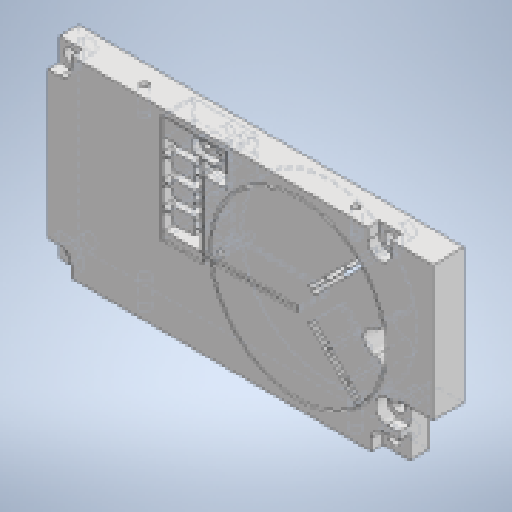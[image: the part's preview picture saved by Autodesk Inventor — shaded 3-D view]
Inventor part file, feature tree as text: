
AUTODESK INVENTOR PART (.ipt)
format: ipt  version: 2023 (Build 270158000, 158)  size: 611,328 bytes
history: native  units: mm
features: extrude x11, sketch x11, other x7, reference x7, fillet x1
ambient origin geometry x8: Origin, YZ Plane, XZ Plane, XY Plane, X Axis, Y Axis, Z Axis, Center Point
bodies: Solid1 (feature_tree)
feature tree (37):
  other  "<userpath>\ClawdDrive\Objet3D\IminaProbe\V3Roue\Settings.xlsx"
  extrude  "Extrusion1"  Depth=9.0mm
  extrude  "Extrusion2"  Depth=9.0mm TaperAngle=0.0deg
  extrude  "Extrusion3"  Depth=40.0mm
  fillet  "Fillet1"  Radius=1.6mm
  extrude  "Extrusion4"  Depth=45.0mm
  extrude  "Extrusion5"  TaperAngle=45.0deg  [1 undecoded]
  extrude  "Extrusion6"  Depth=10.0mm
  extrude  "Extrusion7"  Depth=1.0mm
  extrude  "Extrusion8"  Depth=1.0mm
  extrude  "Extrusion9"  Depth=0.05mm
  extrude  "Extrusion10"  Depth=0.1mm
  extrude  "Extrusion11"  Depth=10.0mm TaperAngle=0.0deg
  sketch  "Sketch1"  dims[d0=8.0mm d1=0.0mm d2=9.0mm]
  reference  "Reference1"
  sketch  "Sketch2"  dims[d3=15.0mm d4=9.0mm d5=0.0mm]
  sketch  "Sketch3"  dims[d6=15.0mm d7=40.0mm d8=1.6mm]
  sketch  "Sketch4"  dims[d9=6.0mm d10=45.0mm]
  sketch  "Sketch5"  dims[d11=20.0mm d12=45.0deg]
  sketch  "Sketch7"  dims[d13=45.0deg d14=10.0mm]
  reference  "Reference2"
  reference  "Reference3"
  sketch  "Sketch8"  dims[d15=46.0mm d16=1.0mm]
  sketch  "Sketch10"  dims[d17=1.0mm d18=1.0mm]
  sketch  "Sketch11"  dims[d19=1.0mm d20=0.05mm]
  sketch  "Sketch12"  dims[d21=0.1mm d22=0.1mm]
  reference  "Reference6"
  reference  "Reference7"
  sketch  "Sketch13"  dims[d23=0.05mm d24=8.0mm d25=0.0mm d26=2.0mm d33=2.65mm d34=0.4mm d35=0.5mm d36=0.5mm d37=20.0mm d38=1.75mm d39=1.6mm d40=25.0mm d41=0.0mm d42=0.5mm d43=0.5mm d44=0.5mm d45=0.5mm d47=1.5mm d48=0.0mm d49=0.1mm d50=0.1mm d51=0.5mm d52=0.5mm d53=0.5mm d54=18.0mm d56=0.0mm d57=1.5mm d58=0.1mm d59=8.0mm d60=0.0mm d61=8.0mm d62=0.0mm d63=16.0mm d64=2.4mm d65=2.4mm d66=8.0mm d67=0.0mm d68=3.0mm d69=14.0mm d70=3.0mm d72=3.0mm d73=3.4mm d74=3.4mm d75=3.4mm d76=3.0mm d77=3.0mm d78=3.0mm d79=4.0mm d80=3.4mm d81=3.0mm d82=3.4mm d83=11.0mm d84=8.0mm d85=0.0mm d86=6.0mm d87=6.0mm d88=6.0mm d89=6.0mm d90=6.0mm d91=3.0mm d92=0.0mm d93=4.0mm d94=4.0mm d95=2.0mm d96=0.0mm d97=7.0mm d98=0.0mm d99=2.05mm d100=2.75mm d101=2.05mm d102=2.05mm d103=2.05mm d104=2.05mm d105=2.05mm d106=7.0mm d107=0.0mm d108=10.0mm d109=23.0mm d110=55.0mm d111=55.0mm d112=2.05mm d113=23.0mm d114=55.0mm d116=5.0mm d117=2.0mm d118=5.0mm d119=2.0mm d120=5.0mm d121=2.0mm d122=5.0mm d123=2.0mm d125=1.0mm d126=1.0mm d127=2.1mm d129=2.0mm d130=2.0mm d132=2.1mm d134=2.0mm d135=2.0mm d136=2.0mm d137=2.0mm d138=2.0mm d139=2.1mm d140=2.1mm d141=4.0mm d142=4.0mm d143=3.0mm d144=4.0mm d145=3.0mm d146=4.0mm d148=2.1mm d150=2.100022mm d151=2.699978mm d152=2.0mm d153=2.0mm]
  reference  "Reference10"
  reference  "Reference11"
  other  "<userpath>\ClawdDrive\Objet3D\IminaProbe\V3Roue\RoueV3.iam"
  other  "RoueV3.iam"
  other  "RoueV3PartB:1"
  other  "AngleScrewBlocActuator:1"
  other  "DifferentialLinearActuator:13"
  other  "DifferentialLinearActuator:14"
note: 1 required parameter value undecoded (feature->parameter linkage not recoverable at this tier; creation-order binding heuristic only, values carry confidence <= 0.55)
